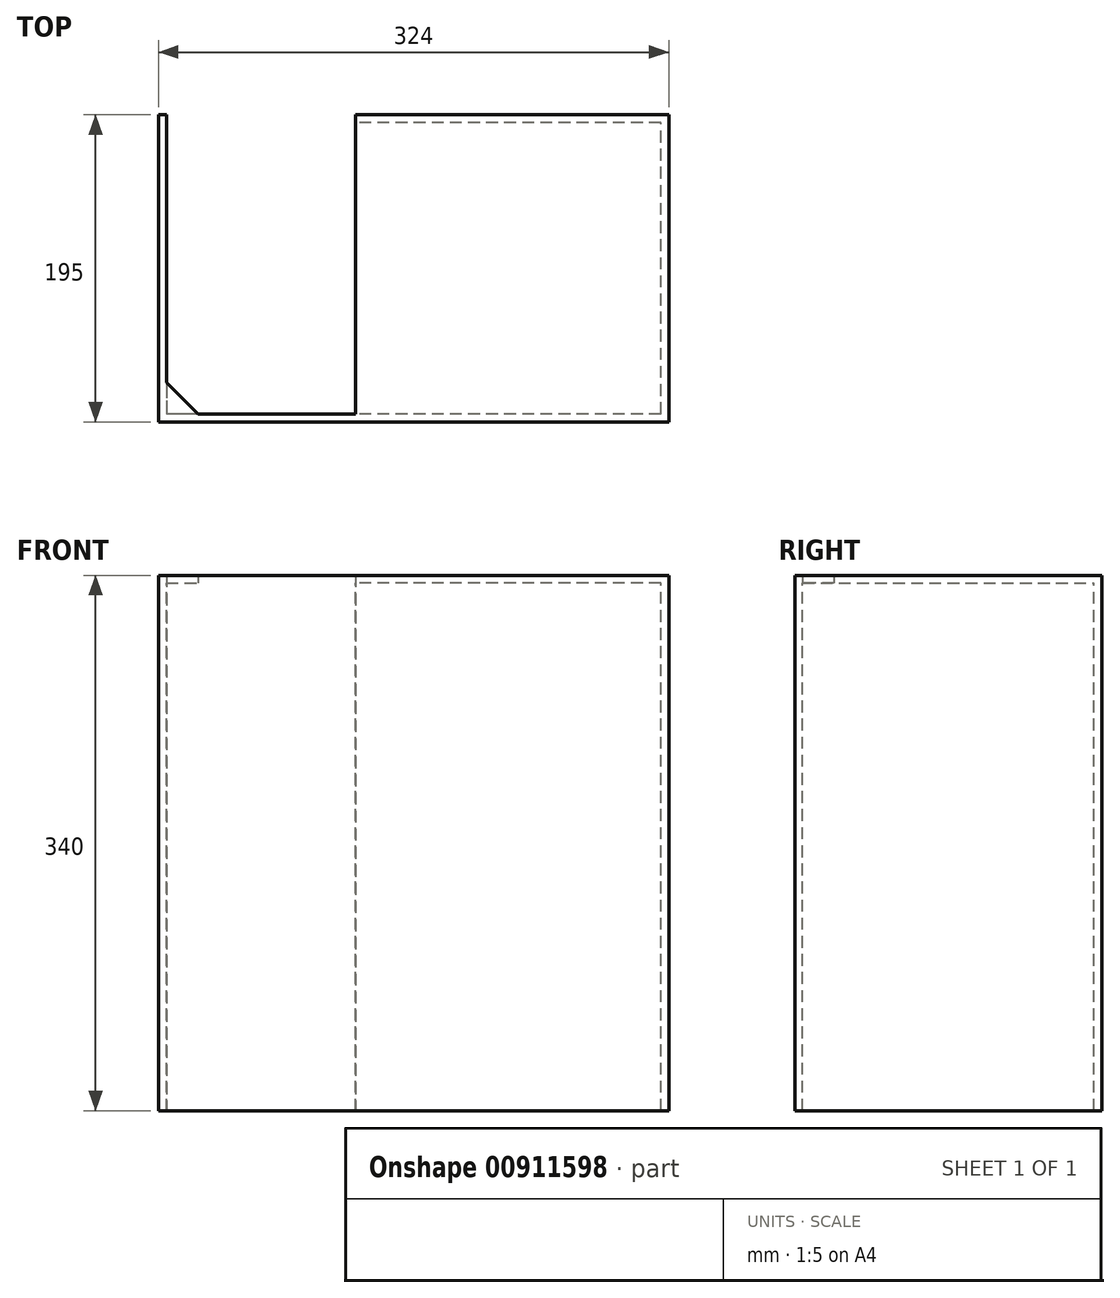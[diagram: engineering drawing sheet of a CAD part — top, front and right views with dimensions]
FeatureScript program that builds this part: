
annotation { "Feature Type Name" : "Feature", "Feature Type Description" : "" }
export const myFeature = defineFeature(function(context is Context, id is Id, definition is map)
    precondition{}
    {
        {
            var Q0;
            Q0=qCreatedBy(makeId("Top.planeOp"),FACE);
            var sketch = newSketch(context, id + "F0", { "sketchPlane" : qUnion([Q0])});
            skLineSegment(sketch, "E0.bottom", {"start": v(0, 0) * mm, "end": v(-324, 0) * mm});
            skLineSegment(sketch, "E0.top", {"start": v(0, 195) * mm, "end": v(-199, 195) * mm});
            skLineSegment(sketch, "E0.left", {"start": v(0, 0) * mm, "end": v(0, 195) * mm});
            skLineSegment(sketch, "E0.right", {"start": v(-324, 0) * mm, "end": v(-324, 195) * mm});
            skLineSegment(sketch, "E1", {"start": v(-319, 195) * mm, "end": v(-319, 25) * mm});
            skLineSegment(sketch, "E2", {"start": v(-319, 25) * mm, "end": v(-299, 5) * mm});
            skLineSegment(sketch, "E3", {"start": v(-299, 5) * mm, "end": v(-199, 5) * mm});
            skLineSegment(sketch, "E4", {"start": v(-199, 5) * mm, "end": v(-199, 195) * mm});
            skLineSegment(sketch, "E5.trimOffspring", {"start": v(-319, 195) * mm, "end": v(-324, 195) * mm});
            skSolve(sketch);
        }
        {
            var Q0;
            Q0=makeQuery(id+"F0.imprint","IMPRINT",FACE,{"disambiguationData":[TD([[makeQuery(id+"F0.imprint","IMPRINT",EDGE,{"derivedFrom":sQuery(id+"F0.wireOp",EDGE,"E0.bottom")}),-1.0]])]});
            extrude(context, id + "F1", {"entities" : qUnion([Q0]), "depth" : 5 * mm, "offsetDistance" : 25 * mm});
        }
        {
            var Q0;
            Q0=makeQuery(id+"F1.opExtrude","CAP_FACE",FACE,{"disambiguationData":[OSD([sQuery(id+"F0.wireOp",EDGE,"E0.bottom"),sQuery(id+"F0.wireOp",EDGE,"E0.top"),sQuery(id+"F0.wireOp",EDGE,"E0.left"),sQuery(id+"F0.wireOp",EDGE,"E0.right"),sQuery(id+"F0.wireOp",EDGE,"E1"),sQuery(id+"F0.wireOp",EDGE,"E2"),sQuery(id+"F0.wireOp",EDGE,"E3"),sQuery(id+"F0.wireOp",EDGE,"E4"),sQuery(id+"F0.wireOp",EDGE,"E5.trimOffspring")])],"isStart":true});
            var sketch = newSketch(context, id + "F2", { "sketchPlane" : qUnion([Q0])});
            skLineSegment(sketch, "E6.0", {"start": v(-324, 0) * mm, "end": v(-324, -195) * mm});
            skLineSegment(sketch, "E7.0", {"start": v(-319, -195) * mm, "end": v(-324, -195) * mm});
            skLineSegment(sketch, "E8.0", {"start": v(-319, -195) * mm, "end": v(-319, -25) * mm});
            skLineSegment(sketch, "E9", {"start": v(-319, -25) * mm, "end": v(-319, 0) * mm});
            skLineSegment(sketch, "E10", {"start": v(-319, 0) * mm, "end": v(-324, 0) * mm});
            skSolve(sketch);
        }
        {
            var Q0;
            Q0 = qSketchRegion(id + "F2", true);
            extrude(context, id + "F3", {"entities" : qUnion([Q0]), "operationType" : NewBodyOperationType.ADD, "depth" : 335 * mm, "offsetDistance" : 25 * mm});
        }
        {
            var Q0;
            Q0=makeQuery(id+"F3.boolean.opBoolean","MERGE",FACE,{"derivedFrom":[makeQuery(id+"F1.opExtrude","SWEPT_FACE",FACE,{"disambiguationData":[OSD([sQuery(id+"F0.wireOp",EDGE,"E1")])]}),makeQuery(id+"F3.opExtrude","SWEPT_FACE",FACE,{"disambiguationData":[OSD([sQuery(id+"F2.wireOp",EDGE,"E8.0"),sQuery(id+"F2.wireOp",EDGE,"E9")])]})]});
            var sketch = newSketch(context, id + "F4", { "sketchPlane" : qUnion([Q0])});
            skLineSegment(sketch, "E11.0", {"start": v(0, -335) * mm, "end": v(0, 0) * mm});
            skLineSegment(sketch, "E12.0", {"start": v(195, -335) * mm, "end": v(0, -335) * mm});
            skLineSegment(sketch, "E13", {"start": v(5, -335) * mm, "end": v(5, 0) * mm});
            skPoint(sketch, "E13.endSnap0", {"position": v(12.5, 0) * mm});
            skLineSegment(sketch, "E14", {"start": v(5, 0) * mm, "end": v(0, 0) * mm});
            skSolve(sketch);
        }
        {
            var Q0;
            Q0 = qSketchRegion(id + "F4", true);
            var Q1;
            Q1=makeQuery(id+"F1.opExtrude","SWEPT_FACE",FACE,{"disambiguationData":[OSD([sQuery(id+"F0.wireOp",EDGE,"E0.left")])]});
            extrude(context, id + "F5", {"entities" : qUnion([Q0]), "operationType" : NewBodyOperationType.ADD, "endBound" : BoundingType.UP_TO_SURFACE, "depth" : 25 * mm, "endBoundEntityFace" : qUnion([Q1]), "offsetDistance" : 25 * mm});
        }
        {
            var Q0;
            {var subQ0=sQuery(id+"F0.wireOp",EDGE,"E4");var subQ1=sQuery(id+"F0.wireOp",EDGE,"E0.left");var subQ2=sQuery(id+"F0.wireOp",EDGE,"E3");var subQ4=sQuery(id+"F0.wireOp",EDGE,"E0.top");Q0=makeQuery(id+"F5.boolean.opBoolean","SPLIT",FACE,{"disambiguationData":[TD([makeQuery(id+"F1.opExtrude","SWEPT_FACE",FACE,{"disambiguationData":[OSD([subQ4])]})])],"derivedFrom":makeQuery(id+"F1.opExtrude","CAP_FACE",FACE,{"disambiguationData":[OSD([sQuery(id+"F0.wireOp",EDGE,"E0.bottom"),subQ4,subQ1,sQuery(id+"F0.wireOp",EDGE,"E0.right"),sQuery(id+"F0.wireOp",EDGE,"E1"),sQuery(id+"F0.wireOp",EDGE,"E2"),subQ2,subQ0,sQuery(id+"F0.wireOp",EDGE,"E5.trimOffspring")])],"isStart":true})});}
            var sketch = newSketch(context, id + "F6", { "sketchPlane" : qUnion([Q0])});
            skLineSegment(sketch, "E15.0", {"start": v(0, -5) * mm, "end": v(0, -195) * mm});
            skLineSegment(sketch, "E16.0", {"start": v(0, -195) * mm, "end": v(-199, -195) * mm});
            skLineSegment(sketch, "E17.0", {"start": v(-5, -190) * mm, "end": v(-199, -190) * mm});
            skLineSegment(sketch, "E17.1", {"start": v(-5, -5) * mm, "end": v(-5, -190) * mm});
            skLineSegment(sketch, "E18", {"start": v(-5, -5) * mm, "end": v(0, -5) * mm});
            skLineSegment(sketch, "E19", {"start": v(-199, -190) * mm, "end": v(-199, -195) * mm});
            skSolve(sketch);
        }
        {
            var Q0;
            Q0 = qSketchRegion(id + "F6", true);
            var Q1;
            Q1=makeQuery(id+"F5.boolean.opBoolean","MERGE",FACE,{"derivedFrom":[makeQuery(id+"F3.opExtrude","CAP_FACE",FACE,{"disambiguationData":[OSD([sQuery(id+"F2.wireOp",EDGE,"E6.0"),sQuery(id+"F2.wireOp",EDGE,"E7.0"),sQuery(id+"F2.wireOp",EDGE,"E8.0"),sQuery(id+"F2.wireOp",EDGE,"E9"),sQuery(id+"F2.wireOp",EDGE,"E10")])],"isStart":false}),makeQuery(id+"F5.opExtrude","SWEPT_FACE",FACE,{"disambiguationData":[OSD([sQuery(id+"F4.wireOp",EDGE,"E12.0")])]})]});
            extrude(context, id + "F7", {"entities" : qUnion([Q0]), "operationType" : NewBodyOperationType.ADD, "endBound" : BoundingType.UP_TO_SURFACE, "depth" : 25 * mm, "endBoundEntityFace" : qUnion([Q1]), "offsetDistance" : 25 * mm});
        }
    });
